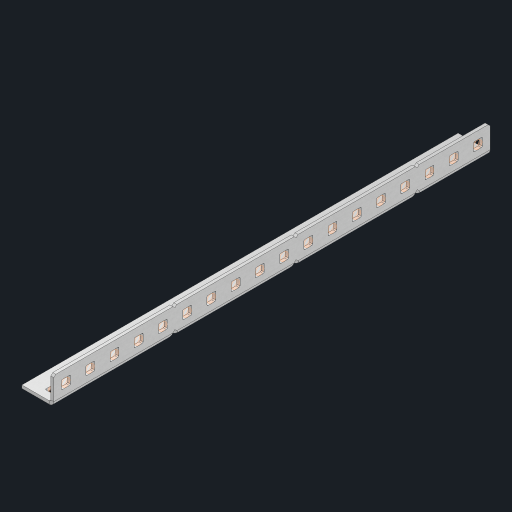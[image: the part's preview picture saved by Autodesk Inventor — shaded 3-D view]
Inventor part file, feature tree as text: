
AUTODESK INVENTOR PART (.ipt)
format: ipt  version: 2023 (Build 270158000, 158)  size: 730,112 bytes
history: native  units: in
note: dims shown in document units (in); Inventor stores cm internally (conversion verified against a paired STEP export)
features: other x41, extrude x35, sheet_metal_op x10, sketch x8, mirror x1, pattern_linear x1, chamfer x1
ambient origin geometry x8: Origin, YZ Plane, XZ Plane, XY Plane, X Axis, Y Axis, Z Axis, Center Point
bodies: Solid1 (feature_tree), Body (feature_tree)
feature tree (97):
  other  "Flange Pattern Plane"
  sheet_metal_op  "Flange Pattern"
  sheet_metal_op  "Body Pattern"
  other  "Arc Length"
  mirror  "Notch Mirror"
  pattern_linear  "Notch Pattern"  Spacing1=0.25in  [1 undecoded]
  chamfer  "End Chamfer"
  extrude  "Half Cut"  Depth=0.0625in
  sketch  "Sketch1"  dims[d0=1.5in]
  other  "Plate1"
  sketch  "Sketch2"  dims[d1=9.0in]
  other  "Plate2"
  sheet_metal_op  "Bend1"
  sheet_metal_op  "Corner1"
  sketch  "Sketch3"  dims[d2=0.0625in]
  other  "Flange Pattern Sketch"
  sketch  "Sketch7"  dims[d3=0.0625in]
  other  "Srf1"
  other  "Srf2"
  sketch  "Sketch8"  dims[d4=0.0312in]
  sketch  "Sketch9"  dims[d5=0.125in]
  other  "Srf91"
  sheet_metal_op  "Body Pattern Sketch"
  other  "Srf92"
  sketch  "Sketch13"  dims[d6=0.0625in]
  sketch  "Sketch14"  dims[d7=0.5in d8=90.0deg d9=0.0312in d10=0.25in d11=0.0625in d12=0.0625in d16=0.182in d17=0.02in d18=0.0625in d19=0.0in d20=0.25in d21=0.25in d46=0.172in d47=1.0in d48=0.0in d49=0.182in d50=0.02in d51=0.25in d52=0.25in d53=0.0625in d54=0.0in d55=0.172in d56=1.0in d57=0.0in d60=7.0866in d62=0.5in d63=0.3937in d65=0.5in d85=0.1473in d86=0.1782in d88=0.04in d89=0.0625in d90=0.0in d91=0.04in d92=0.0491in d95=2.5in d96=0.04in d97=0.25in d98=45.0deg d101=0.0in d102=2.497in d131=0.5in d132=7.0866in d134=0.5in d139=0.5in]
  other  "Srf856"
  other  "Srf1310"
  other  "Srf1311"
  other  "Srf1312"
  other  "Srf1376"
  other  "Srf1377"
  other  "Srf1728"
  other  "Srf1755"
  other  "Srf1878"
  other  "Srf1879"
  other  "Srf1880"
  other  "Srf1881"
  other  "Srf1882"
  other  "Srf1883"
  other  "Srf1884"
  other  "Srf1885"
  other  "Srf1886"
  other  "Srf1887"
  other  "Srf1888"
  other  "Srf1889"
  other  "Srf1942"
  other  "Srf1943"
  other  "Srf1944"
  other  "Srf1945"
  other  "Srf1946"
  other  "Srf1947"
  other  "Srf1948"
  other  "Srf1949"
  other  "Srf1950"
  other  "Srf1951"
  other  "Srf1952"
  other  "Srf1953"
  sheet_metal_op  "Flange Stamp"
  sheet_metal_op  "Flange Circle"
  sheet_metal_op  "Body Stamp"
  sheet_metal_op  "Body Circle"
  sheet_metal_op  "Notch"
  extrude  "ExtrusionSrf2"  Depth=0.0625in
  extrude  "ExtrusionSrf92"  Depth=0.5in
  extrude  "ExtrusionSrf856"  Depth=0.02in
  extrude  "ExtrusionSrf1310"  Depth=0.0625in
  extrude  "ExtrusionSrf1311"  TaperAngle=0.0deg  [1 undecoded]
  extrude  "ExtrusionSrf1312"  Depth=0.5in
  extrude  "ExtrusionSrf1376"  Depth=0.5in
  extrude  "ExtrusionSrf1377"  Depth=0.5in
  extrude  "ExtrusionSrf1728"  Depth=0.5in TaperAngle=0.0deg
  extrude  "ExtrusionSrf1755"  Depth=0.5in
  extrude  "ExtrusionSrf1878"  Depth=0.02in
  extrude  "ExtrusionSrf1879"  Depth=0.5in
  extrude  "ExtrusionSrf1880"  Depth=0.5in
  extrude  "ExtrusionSrf1881"  Depth=0.0625in
  extrude  "ExtrusionSrf1882"  TaperAngle=0.0deg  [1 undecoded]
  extrude  "ExtrusionSrf1883"  Depth=0.5in
  extrude  "ExtrusionSrf1884"  Depth=0.5in TaperAngle=0.0deg
  extrude  "ExtrusionSrf1885"  Depth=0.5in
  extrude  "ExtrusionSrf1886"  Depth=0.5in
  extrude  "ExtrusionSrf1887"  Depth=0.5in
  extrude  "ExtrusionSrf1888"  Depth=0.5in
  extrude  "ExtrusionSrf1889"  Depth=0.5in
  extrude  "ExtrusionSrf1942"  Depth=0.0625in
  extrude  "ExtrusionSrf1943"  TaperAngle=0.0deg  [1 undecoded]
  extrude  "ExtrusionSrf1944"  Depth=0.5in
  extrude  "ExtrusionSrf1945"  Depth=0.5in
  extrude  "ExtrusionSrf1946"  Depth=0.5in
  extrude  "ExtrusionSrf1947"  Depth=0.5in TaperAngle=45.0deg
  extrude  "ExtrusionSrf1948"  TaperAngle=0.0deg  [1 undecoded]
  extrude  "ExtrusionSrf1949"  Depth=0.5in
  extrude  "ExtrusionSrf1950"  Depth=0.5in
  extrude  "ExtrusionSrf1951"  Depth=0.5in
  extrude  "ExtrusionSrf1952"  Depth=0.5in
  extrude  "ExtrusionSrf1953"  Depth=0.5in
note: 5 required parameter values undecoded (feature->parameter linkage not recoverable at this tier; creation-order binding heuristic only, values carry confidence <= 0.55)
